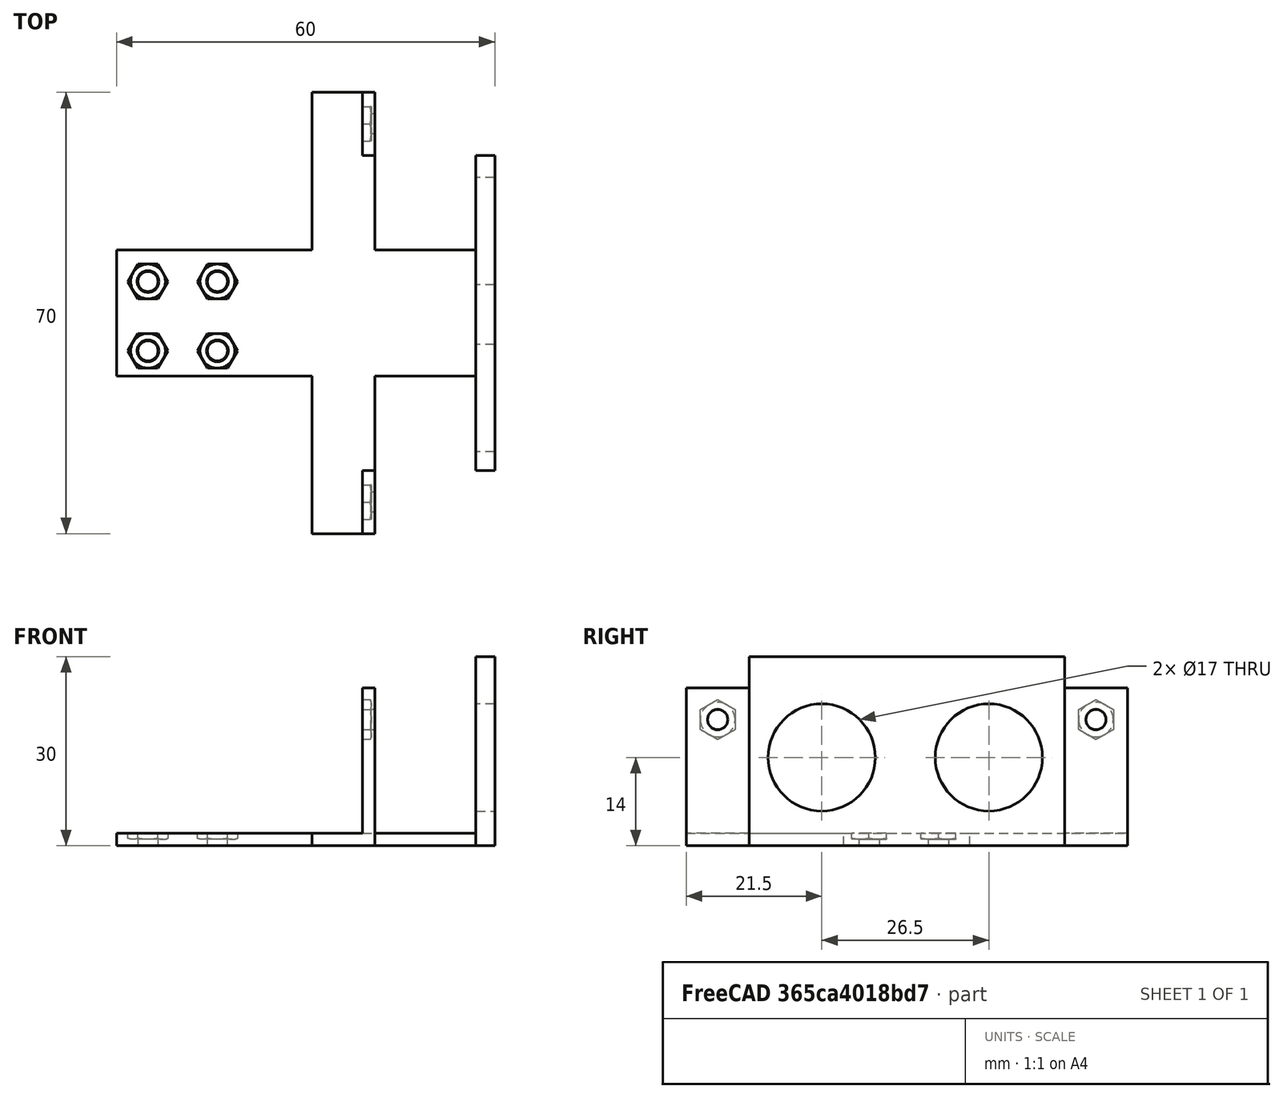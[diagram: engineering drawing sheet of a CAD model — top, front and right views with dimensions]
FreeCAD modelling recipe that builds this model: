
FCSTD DOCUMENT  (FreeCAD 0.21R33771 (Git))
Label: soporteSensores
License: All rights reserved
LicenseURL: http://en.wikipedia.org/wiki/All_rights_reserved
objects: Part::Cylinder×8, Part::MultiFuse×8, Part::FeaturePython×6, Part::Box×5, Part::Cut×4, Mesh::Feature×1
note: 31 computed .brp shape members not serialized (recipe doc carries the construction recipe); baked Part::Feature solids carry a one-line shape summary decoded from their .brp

FEATURE [Part::Box] Box028  label="Cubo028"
  AttacherType = Attacher::AttachEngine3D
  Height = 2
  Length = 60
  Placement = pos=(21,-10,-11) rot=(0,0,1;0rad)
  Width = 20
FEATURE [Part::Box] Box030  label="Cubo030"
  AttacherType = Attacher::AttachEngine3D
  Height = 30
  Length = 3
  Placement = pos=(78,-25,-11) rot=(0,0,1;0rad)
  Width = 50
FEATURE [Part::Box] Box031  label="Cubo031"
  AttacherType = Attacher::AttachEngine3D
  Height = 2
  Length = 10
  Placement = pos=(52,-35,-11) rot=(0,0,1;0rad)
  Width = 70
FEATURE [Part::Box] Box032  label="Cubo032"
  AttacherType = Attacher::AttachEngine3D
  Height = 25
  Length = 2
  Placement = pos=(60,-35,-11) rot=(0,0,1;0rad)
  Width = 10
FEATURE [Part::Box] Box033  label="Cubo033"
  AttacherType = Attacher::AttachEngine3D
  Height = 25
  Length = 2
  Placement = pos=(60,-35,-11) rot=(0,0,1;0rad)
  Width = 10
FEATURE [Part::Cylinder] Cylinder083  label="Cilindro083"
  Angle = 360
  AttacherType = Attacher::AttachEngine3D
  FirstAngle = 0
  Height = 10
  Placement = pos=(26,5,-18) rot=(0,0,1;0rad)
  Radius = 1.6
  SecondAngle = 0
FEATURE [Part::Cylinder] Cylinder084  label="Cilindro084"
  Angle = 360
  AttacherType = Attacher::AttachEngine3D
  FirstAngle = 0
  Height = 10
  Placement = pos=(26,-6,-18) rot=(0,0,1;0rad)
  Radius = 1.6
  SecondAngle = 0
FEATURE [Part::Cylinder] Cylinder085  label="Cilindro085"
  Angle = 360
  AttacherType = Attacher::AttachEngine3D
  FirstAngle = 0
  Height = 10
  Placement = pos=(37,-6,-18) rot=(0,0,1;0rad)
  Radius = 1.6
  SecondAngle = 0
FEATURE [Part::Cylinder] Cylinder086  label="Cilindro086"
  Angle = 360
  AttacherType = Attacher::AttachEngine3D
  FirstAngle = 0
  Height = 10
  Placement = pos=(37,5,-18) rot=(0,0,1;0rad)
  Radius = 1.6
  SecondAngle = 0
FEATURE [Part::Cylinder] Cylinder087  label="Cilindro087"
  Angle = 360
  AttacherType = Attacher::AttachEngine3D
  FirstAngle = 0
  Height = 10
  Placement = pos=(75,-13.5,3) rot=(0,1,0;1.5708rad)
  Radius = 8.5
  SecondAngle = 0
FEATURE [Part::Cylinder] Cylinder088  label="Cilindro088"
  Angle = 360
  AttacherType = Attacher::AttachEngine3D
  FirstAngle = 0
  Height = 11
  Placement = pos=(75,13,3) rot=(0,1,0;1.5708rad)
  Radius = 8.5
  SecondAngle = 0
FEATURE [Part::Cylinder] Cylinder089  label="Cilindro089"
  Angle = 360
  AttacherType = Attacher::AttachEngine3D
  FirstAngle = 0
  Height = 10
  Placement = pos=(57,-31,-4) rot=(0,1,0;1.5708rad)
  Radius = 1.6
  SecondAngle = 0
FEATURE [Part::Cylinder] Cylinder090  label="Cilindro090"
  Angle = 360
  AttacherType = Attacher::AttachEngine3D
  FirstAngle = 0
  Height = 10
  Placement = pos=(57,-31,-4) rot=(0,1,0;1.5708rad)
  Radius = 1.6
  SecondAngle = 0
FEATURE [Part::MultiFuse] Fusion042
  Shapes = -> [Cylinder086,Cylinder083,Cylinder084,Cylinder085]
FEATURE [Part::MultiFuse] Fusion043
  Shapes = -> [Cylinder088,Cylinder087]
FEATURE [Part::Cut] Cut023
  Base = -> Box030
  Tool = -> Fusion043
FEATURE [Part::MultiFuse] Fusion044
  Shapes = -> [Box028,Cut023]
FEATURE [Part::FeaturePython] Nut023  label="M3-Tuerca023"  # Fasteners workbench fastener (typed FeaturePython)
  Placement = pos=(59,-31,-4) rot=(0,1,0;1.5708rad)
  diameter = 4
  invert = false
  leftHanded = false
  matchOuter = false
  offset = 0
  thread = false
  type = 22
FEATURE [Part::MultiFuse] Fusion045
  Placement = pos=(0,1,13) rot=(0,0,1;0rad)
  Shapes = -> [Cylinder089,Nut023]
FEATURE [Part::Cut] Cut024
  Base = -> Box032
  Tool = -> Fusion045
FEATURE [Part::FeaturePython] Nut024  label="M3-Tuerca024"  # Fasteners workbench fastener (typed FeaturePython)
  Placement = pos=(59,-31,-4) rot=(0,1,0;1.5708rad)
  diameter = 4
  invert = false
  leftHanded = false
  matchOuter = false
  offset = 0
  thread = false
  type = 22
FEATURE [Part::MultiFuse] Fusion046
  Placement = pos=(0,1,13) rot=(0,0,1;0rad)
  Shapes = -> [Cylinder090,Nut024]
FEATURE [Part::Cut] Cut025
  Base = -> Box033
  Placement = pos=(0,60,0) rot=(0,0,1;0rad)
  Tool = -> Fusion046
FEATURE [Part::MultiFuse] Fusion047
  Shapes = -> [Cut024,Cut025,Box031,Fusion044]
FEATURE [Part::FeaturePython] Nut  label="M3-Tuerca"  # Fasteners workbench fastener (typed FeaturePython)
  Placement = pos=(37,5,-10) rot=(0,0,1;0rad)
  diameter = 4
  invert = false
  leftHanded = false
  matchOuter = false
  offset = 0
  thread = false
  type = 22
FEATURE [Part::FeaturePython] Nut025  label="M3-Tuerca025"  # Fasteners workbench fastener (typed FeaturePython)
  Placement = pos=(37,-6,-10) rot=(0,0,1;0rad)
  diameter = 4
  invert = false
  leftHanded = false
  matchOuter = false
  offset = 0
  thread = false
  type = 22
FEATURE [Part::FeaturePython] Nut026  label="M3-Tuerca026"  # Fasteners workbench fastener (typed FeaturePython)
  Placement = pos=(26,-6,-10) rot=(0,0,1;0rad)
  diameter = 4
  invert = false
  leftHanded = false
  matchOuter = false
  offset = 0
  thread = false
  type = 22
FEATURE [Part::FeaturePython] Nut027  label="M3-Tuerca027"  # Fasteners workbench fastener (typed FeaturePython)
  Placement = pos=(26,5,-10) rot=(0,0,1;0rad)
  diameter = 4
  invert = false
  leftHanded = false
  matchOuter = false
  offset = 0
  thread = false
  type = 22
FEATURE [Part::MultiFuse] Fusion
  Shapes = -> [Nut027,Nut,Nut025,Nut026]
FEATURE [Part::MultiFuse] Fusion048
  Shapes = -> [Fusion042,Fusion]
FEATURE [Part::Cut] Cut  label="soporteSensores"
  Base = -> Fusion047
  Tool = -> Fusion048
FEATURE [Mesh::Feature] Mesh  label="soporteSensores (Meshed)"
